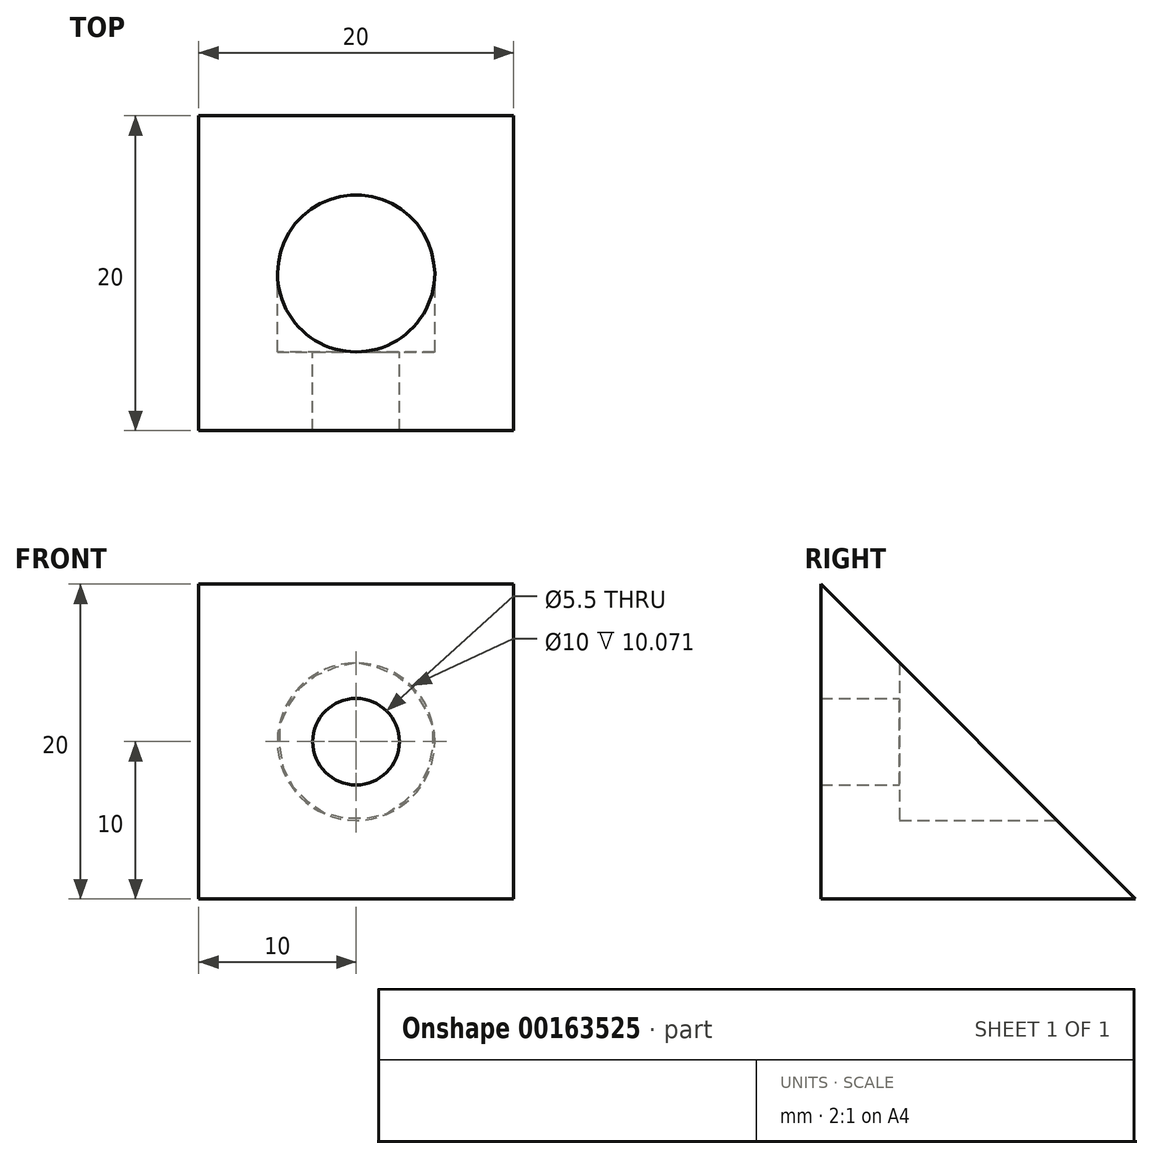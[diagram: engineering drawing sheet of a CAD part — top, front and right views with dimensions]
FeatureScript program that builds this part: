
annotation { "Feature Type Name" : "Feature", "Feature Type Description" : "" }
export const myFeature = defineFeature(function(context is Context, id is Id, definition is map)
    precondition{}
    {
        {
            var Q0;
            Q0=qCreatedBy(makeId("Right.planeOp"),FACE);
            var sketch = newSketch(context, id + "F0", { "sketchPlane" : qUnion([Q0])});
            skLineSegment(sketch, "E0", {"start": v(0, 0) * mm, "end": v(20, 0) * mm});
            skLineSegment(sketch, "E1", {"start": v(0, 0) * mm, "end": v(0, 20) * mm});
            skLineSegment(sketch, "E2", {"start": v(0, 20) * mm, "end": v(20, 0) * mm});
            skSolve(sketch);
        }
        {
            var Q0;
            Q0=makeQuery(id+"F0.imprint","IMPRINT",FACE,{"disambiguationData":[TD([[makeQuery(id+"F0.imprint","IMPRINT",EDGE,{"derivedFrom":sQuery(id+"F0.wireOp",EDGE,"E0")}),1.0]])]});
            extrude(context, id + "F1", {"entities" : qUnion([Q0]), "oppositeDirection" : true, "depth" : 20 * mm});
        }
        {
            var Q0;
            Q0=qCreatedBy(makeId("Front.planeOp"),FACE);
            cPlane(context, id + "F2", {"entities" : qUnion([Q0]), "cplaneType" : CPlaneType.OFFSET, "offset" : 20 * mm, "oppositeDirection" : true, "width" : 150 * mm, "height" : 150 * mm});
        }
        {
            var Q0;
            Q0=qCreatedBy(id+"F2.planeOp",FACE);
            var sketch = newSketch(context, id + "F3", { "sketchPlane" : qUnion([Q0])});
            skLineSegment(sketch, "E3", {"start": v(-20, 20) * mm, "end": v(0, 0) * mm, "construction": true});
            skLineSegment(sketch, "E4", {"start": v(-20, 0) * mm, "end": v(0, 20) * mm, "construction": true});
            skPoint(sketch, "E5", {"position": v(-10, 10) * mm});
            skCircle(sketch, "E6", {"center": v(-10, 10) * mm, "radius": 5 * mm});
            skSolve(sketch);
        }
        {
            var Q0;
            Q0=sQuery(id+"F3.wireOp",VERTEX,"E5");
            var Q1;
            Q1=makeQuery(id+"F1.opExtrude","SWEPT_BODY",BODY,{"disambiguationData":[OSD([sQuery(id+"F0.wireOp",EDGE,"E0"),sQuery(id+"F0.wireOp",EDGE,"E1"),sQuery(id+"F0.wireOp",EDGE,"E2")])]});
            hole(context, id + "F4", {"style" : HoleStyle.SIMPLE, "endStyle" : HoleEndStyle.THROUGH, "oppositeDirection" : true, "standardTappedOrClearance" : lookupTablePath({ "standard" : "ISO", "fit" : "Normal", "size" : "M5", "type" : "Clearance" }), "standardBlindInLast" : lookupTablePath({ "fit" : "Standard", "standard" : "ISO", "size" : "M5", "type" : "Clearance" }), "holeDiameter" : 5.5 * mm, "startFromSketch" : true, "locations" : qUnion([Q0]), "scope" : qUnion([Q1]), "isTappedThrough" : true});
        }
        {
            var Q0;
            Q0=makeQuery(id+"F3.imprint","IMPRINT",FACE,{"disambiguationData":[TD([[makeQuery(id+"F3.imprint","IMPRINT",EDGE,{"derivedFrom":sQuery(id+"F3.wireOp",EDGE,"E6")}),1.0]])]});
            extrude(context, id + "F5", {"entities" : qUnion([Q0]), "operationType" : NewBodyOperationType.REMOVE, "depth" : 15 * mm});
        }
    });
